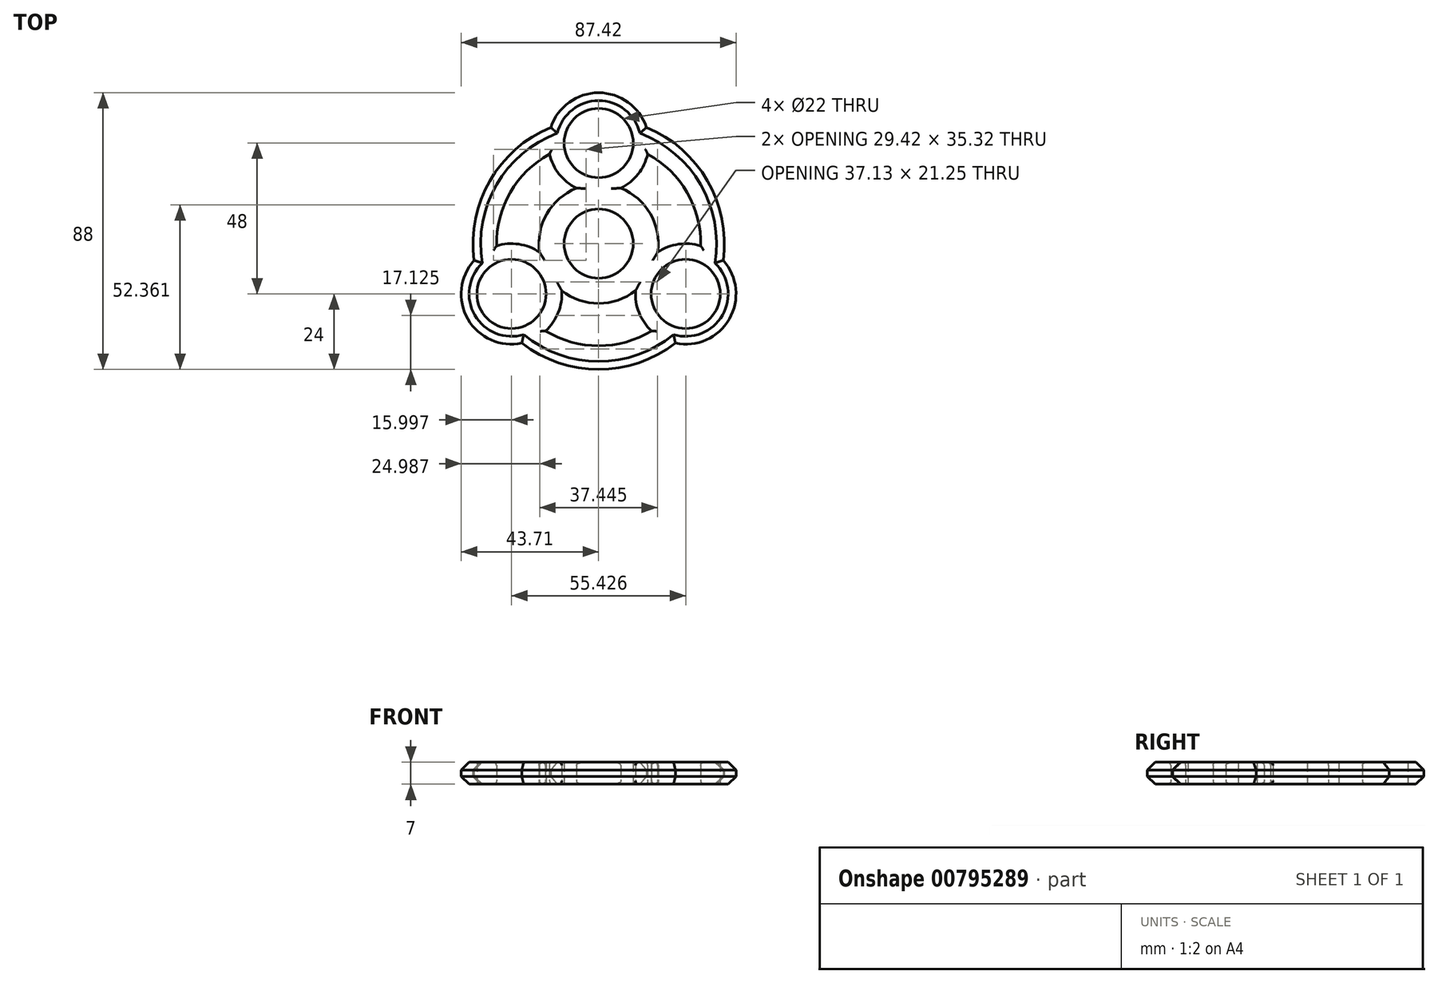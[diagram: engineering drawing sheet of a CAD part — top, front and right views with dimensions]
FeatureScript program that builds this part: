
annotation { "Feature Type Name" : "Feature", "Feature Type Description" : "" }
export const myFeature = defineFeature(function(context is Context, id is Id, definition is map)
    precondition{}
    {
        {
            var Q0;
            Q0=qCreatedBy(makeId("Top.planeOp"),FACE);
            var sketch = newSketch(context, id + "F0", { "sketchPlane" : qUnion([Q0])});
            skCircle(sketch, "E0", {"center": v(0, 0) * mm, "radius": 11 * mm});
            skCircle(sketch, "E1", {"center": v(0, 0) * mm, "radius": 19 * mm});
            skCircle(sketch, "E2", {"center": v(0, 0) * mm, "radius": 40 * mm});
            skCircle(sketch, "E3", {"center": v(0, 0) * mm, "radius": 32.5 * mm});
            skCircle(sketch, "E4", {"center": v(0, 32) * mm, "radius": 11 * mm});
            skCircle(sketch, "E5", {"center": v(0, 32) * mm, "radius": 16 * mm});
            skCircle(sketch, "E6.1.0", {"center": v(-27.71, -16) * mm, "radius": 16 * mm});
            skCircle(sketch, "E6.1.1", {"center": v(-27.71, -16) * mm, "radius": 11 * mm});
            skCircle(sketch, "E6.2.0", {"center": v(27.71, -16) * mm, "radius": 16 * mm});
            skCircle(sketch, "E6.2.1", {"center": v(27.71, -16) * mm, "radius": 11 * mm});
            skSolve(sketch);
        }
        {
            var Q0;
            {var subQ0=sQuery(id+"F0.wireOp",EDGE,"E6.1.0");var subQ1=sQuery(id+"F0.wireOp",EDGE,"E2");var subQ2=makeQuery(id+"F0.imprint","INTERSECT",VERTEX,{"disambiguationData":[OD(0.0)],"derivedFrom":[subQ1,subQ0]});Q0=makeQuery(id+"F0.imprint","IMPRINT",FACE,{"disambiguationData":[TD([[makeQuery(id+"F0.imprint","IMPRINT",EDGE,{"disambiguationData":[TD([[subQ2,-1.0]])],"derivedFrom":subQ1}),1.0]])]});}
            var Q1;
            {var subQ0=sQuery(id+"F0.wireOp",EDGE,"E6.1.0");var subQ1=sQuery(id+"F0.wireOp",EDGE,"E2");var subQ2=makeQuery(id+"F0.imprint","INTERSECT",VERTEX,{"disambiguationData":[OD(1.0)],"derivedFrom":[subQ1,subQ0]});Q1=makeQuery(id+"F0.imprint","IMPRINT",FACE,{"disambiguationData":[TD([[makeQuery(id+"F0.imprint","IMPRINT",EDGE,{"disambiguationData":[TD([[subQ2,1.0]])],"derivedFrom":subQ1}),1.0]])]});}
            var Q2;
            {var subQ0=sQuery(id+"F0.wireOp",EDGE,"E6.1.0");var subQ1=sQuery(id+"F0.wireOp",EDGE,"E2");var subQ2=makeQuery(id+"F0.imprint","INTERSECT",VERTEX,{"disambiguationData":[OD(1.0)],"derivedFrom":[subQ1,subQ0]});Q2=makeQuery(id+"F0.imprint","IMPRINT",FACE,{"disambiguationData":[TD([[makeQuery(id+"F0.imprint","IMPRINT",EDGE,{"disambiguationData":[TD([[subQ2,-1.0]])],"derivedFrom":subQ1}),1.0]])]});}
            var Q3;
            {var subQ0=sQuery(id+"F0.wireOp",EDGE,"E6.1.0");var subQ1=sQuery(id+"F0.wireOp",EDGE,"E2");var subQ2=makeQuery(id+"F0.imprint","INTERSECT",VERTEX,{"disambiguationData":[OD(0.0)],"derivedFrom":[subQ1,subQ0]});Q3=makeQuery(id+"F0.imprint","IMPRINT",FACE,{"disambiguationData":[TD([[makeQuery(id+"F0.imprint","IMPRINT",EDGE,{"disambiguationData":[TD([[subQ2,-1.0]])],"derivedFrom":subQ1}),-1.0]])]});}
            var Q4;
            {var subQ3=sQuery(id+"F0.wireOp",EDGE,"E6.1.0");var subQ5=sQuery(id+"F0.wireOp",EDGE,"E1");var subQ6=makeQuery(id+"F0.imprint","INTERSECT",VERTEX,{"disambiguationData":[OD(0.0)],"derivedFrom":[subQ5,subQ3]});Q4=makeQuery(id+"F0.imprint","IMPRINT",FACE,{"disambiguationData":[TD([[makeQuery(id+"F0.imprint","IMPRINT",EDGE,{"disambiguationData":[TD([[subQ6,-1.0]])],"derivedFrom":subQ5}),-1.0]])]});}
            var Q5;
            {var subQ0=sQuery(id+"F0.wireOp",EDGE,"E6.1.0");var subQ1=sQuery(id+"F0.wireOp",EDGE,"E1");var subQ2=makeQuery(id+"F0.imprint","INTERSECT",VERTEX,{"disambiguationData":[OD(0.0)],"derivedFrom":[subQ1,subQ0]});Q5=makeQuery(id+"F0.imprint","IMPRINT",FACE,{"disambiguationData":[TD([[makeQuery(id+"F0.imprint","IMPRINT",EDGE,{"disambiguationData":[TD([[subQ2,-1.0]])],"derivedFrom":subQ1}),1.0]])]});}
            var Q6;
            Q6=makeQuery(id+"F0.imprint","IMPRINT",FACE,{"disambiguationData":[TD([[makeQuery(id+"F0.imprint","IMPRINT",EDGE,{"derivedFrom":sQuery(id+"F0.wireOp",EDGE,"E0")}),-1.0]])]});
            var Q7;
            {var subQ0=sQuery(id+"F0.wireOp",EDGE,"E6.2.0");var subQ1=sQuery(id+"F0.wireOp",EDGE,"E1");var subQ2=makeQuery(id+"F0.imprint","INTERSECT",VERTEX,{"disambiguationData":[OD(0.0)],"derivedFrom":[subQ1,subQ0]});Q7=makeQuery(id+"F0.imprint","IMPRINT",FACE,{"disambiguationData":[TD([[makeQuery(id+"F0.imprint","IMPRINT",EDGE,{"disambiguationData":[TD([[subQ2,-1.0]])],"derivedFrom":subQ1}),1.0]])]});}
            var Q8;
            {var subQ0=sQuery(id+"F0.wireOp",EDGE,"E6.2.0");var subQ1=sQuery(id+"F0.wireOp",EDGE,"E1");var subQ9=makeQuery(id+"F0.imprint","INTERSECT",VERTEX,{"disambiguationData":[OD(0.0)],"derivedFrom":[subQ1,subQ0]});Q8=makeQuery(id+"F0.imprint","IMPRINT",FACE,{"disambiguationData":[TD([[makeQuery(id+"F0.imprint","IMPRINT",EDGE,{"disambiguationData":[TD([[subQ9,-1.0]])],"derivedFrom":subQ1}),-1.0]])]});}
            var Q9;
            {var subQ0=sQuery(id+"F0.wireOp",EDGE,"E6.2.0");var subQ1=sQuery(id+"F0.wireOp",EDGE,"E2");var subQ2=makeQuery(id+"F0.imprint","INTERSECT",VERTEX,{"disambiguationData":[OD(0.0)],"derivedFrom":[subQ1,subQ0]});Q9=makeQuery(id+"F0.imprint","IMPRINT",FACE,{"disambiguationData":[TD([[makeQuery(id+"F0.imprint","IMPRINT",EDGE,{"disambiguationData":[TD([[subQ2,-1.0]])],"derivedFrom":subQ1}),1.0]])]});}
            var Q10;
            {var subQ0=sQuery(id+"F0.wireOp",EDGE,"E6.2.0");var subQ1=sQuery(id+"F0.wireOp",EDGE,"E2");var subQ2=makeQuery(id+"F0.imprint","INTERSECT",VERTEX,{"disambiguationData":[OD(1.0)],"derivedFrom":[subQ1,subQ0]});Q10=makeQuery(id+"F0.imprint","IMPRINT",FACE,{"disambiguationData":[TD([[makeQuery(id+"F0.imprint","IMPRINT",EDGE,{"disambiguationData":[TD([[subQ2,1.0]])],"derivedFrom":subQ1}),1.0]])]});}
            var Q11;
            {var subQ0=sQuery(id+"F0.wireOp",EDGE,"E5");var subQ1=sQuery(id+"F0.wireOp",EDGE,"E2");var subQ2=makeQuery(id+"F0.imprint","INTERSECT",VERTEX,{"disambiguationData":[OD(0.0)],"derivedFrom":[subQ1,subQ0]});Q11=makeQuery(id+"F0.imprint","IMPRINT",FACE,{"disambiguationData":[TD([[makeQuery(id+"F0.imprint","IMPRINT",EDGE,{"disambiguationData":[TD([[subQ2,1.0]])],"derivedFrom":subQ1}),1.0]])]});}
            var Q12;
            {var subQ0=sQuery(id+"F0.wireOp",EDGE,"E6.2.0");var subQ1=sQuery(id+"F0.wireOp",EDGE,"E2");var subQ2=makeQuery(id+"F0.imprint","INTERSECT",VERTEX,{"disambiguationData":[OD(0.0)],"derivedFrom":[subQ1,subQ0]});Q12=makeQuery(id+"F0.imprint","IMPRINT",FACE,{"disambiguationData":[TD([[makeQuery(id+"F0.imprint","IMPRINT",EDGE,{"disambiguationData":[TD([[subQ2,-1.0]])],"derivedFrom":subQ1}),-1.0]])]});}
            var Q13;
            {var subQ0=sQuery(id+"F0.wireOp",EDGE,"E5");var subQ1=sQuery(id+"F0.wireOp",EDGE,"E1");var subQ2=makeQuery(id+"F0.imprint","INTERSECT",VERTEX,{"disambiguationData":[OD(0.0)],"derivedFrom":[subQ1,subQ0]});Q13=makeQuery(id+"F0.imprint","IMPRINT",FACE,{"disambiguationData":[TD([[makeQuery(id+"F0.imprint","IMPRINT",EDGE,{"disambiguationData":[TD([[subQ2,1.0]])],"derivedFrom":subQ1}),1.0]])]});}
            var Q14;
            {var subQ0=sQuery(id+"F0.wireOp",EDGE,"E5");var subQ1=sQuery(id+"F0.wireOp",EDGE,"E2");var subQ2=makeQuery(id+"F0.imprint","INTERSECT",VERTEX,{"disambiguationData":[OD(1.0)],"derivedFrom":[subQ1,subQ0]});Q14=makeQuery(id+"F0.imprint","IMPRINT",FACE,{"disambiguationData":[TD([[makeQuery(id+"F0.imprint","IMPRINT",EDGE,{"disambiguationData":[TD([[subQ2,-1.0]])],"derivedFrom":subQ1}),1.0]])]});}
            var Q15;
            {var subQ0=sQuery(id+"F0.wireOp",EDGE,"E5");var subQ1=sQuery(id+"F0.wireOp",EDGE,"E2");var subQ2=makeQuery(id+"F0.imprint","INTERSECT",VERTEX,{"disambiguationData":[OD(0.0)],"derivedFrom":[subQ1,subQ0]});Q15=makeQuery(id+"F0.imprint","IMPRINT",FACE,{"disambiguationData":[TD([[makeQuery(id+"F0.imprint","IMPRINT",EDGE,{"disambiguationData":[TD([[subQ2,-1.0]])],"derivedFrom":subQ1}),1.0]])]});}
            var Q16;
            {var subQ0=sQuery(id+"F0.wireOp",EDGE,"E5");var subQ1=sQuery(id+"F0.wireOp",EDGE,"E2");var subQ2=makeQuery(id+"F0.imprint","INTERSECT",VERTEX,{"disambiguationData":[OD(1.0)],"derivedFrom":[subQ1,subQ0]});Q16=makeQuery(id+"F0.imprint","IMPRINT",FACE,{"disambiguationData":[TD([[makeQuery(id+"F0.imprint","IMPRINT",EDGE,{"disambiguationData":[TD([[subQ2,1.0]])],"derivedFrom":subQ1}),1.0]])]});}
            var Q17;
            {var subQ0=sQuery(id+"F0.wireOp",EDGE,"E5");var subQ1=sQuery(id+"F0.wireOp",EDGE,"E2");var subQ2=makeQuery(id+"F0.imprint","INTERSECT",VERTEX,{"disambiguationData":[OD(0.0)],"derivedFrom":[subQ1,subQ0]});Q17=makeQuery(id+"F0.imprint","IMPRINT",FACE,{"disambiguationData":[TD([[makeQuery(id+"F0.imprint","IMPRINT",EDGE,{"disambiguationData":[TD([[subQ2,-1.0]])],"derivedFrom":subQ1}),-1.0]])]});}
            var Q18;
            {var subQ0=sQuery(id+"F0.wireOp",EDGE,"E5");var subQ1=sQuery(id+"F0.wireOp",EDGE,"E1");var subQ2=makeQuery(id+"F0.imprint","INTERSECT",VERTEX,{"disambiguationData":[OD(0.0)],"derivedFrom":[subQ1,subQ0]});Q18=makeQuery(id+"F0.imprint","IMPRINT",FACE,{"disambiguationData":[TD([[makeQuery(id+"F0.imprint","IMPRINT",EDGE,{"disambiguationData":[TD([[subQ2,-1.0]])],"derivedFrom":subQ1}),1.0]])]});}
            var Q19;
            {var subQ0=sQuery(id+"F0.wireOp",EDGE,"e3311fa9-2675-4763-9959-c69614a33db8.1.3.0");var subQ1=sQuery(id+"F0.wireOp",EDGE,"E1");var subQ2=makeQuery(id+"F0.imprint","INTERSECT",VERTEX,{"disambiguationData":[OD(0.0)],"derivedFrom":[subQ1,subQ0]});Q19=makeQuery(id+"F0.imprint","IMPRINT",FACE,{"disambiguationData":[TD([[makeQuery(id+"F0.imprint","IMPRINT",EDGE,{"disambiguationData":[TD([[subQ2,1.0]])],"derivedFrom":subQ1}),1.0]])]});}
            var Q20;
            {var subQ0=sQuery(id+"F0.wireOp",EDGE,"e3311fa9-2675-4763-9959-c69614a33db8.1.3.0");var subQ7=sQuery(id+"F0.wireOp",EDGE,"E1");var subQ8=makeQuery(id+"F0.imprint","INTERSECT",VERTEX,{"disambiguationData":[OD(0.0)],"derivedFrom":[subQ7,subQ0]});Q20=makeQuery(id+"F0.imprint","IMPRINT",FACE,{"disambiguationData":[TD([[makeQuery(id+"F0.imprint","IMPRINT",EDGE,{"disambiguationData":[TD([[subQ8,1.0]])],"derivedFrom":subQ7}),-1.0]])]});}
            var Q21;
            {var subQ0=sQuery(id+"F0.wireOp",EDGE,"e3311fa9-2675-4763-9959-c69614a33db8.1.3.0");var subQ1=sQuery(id+"F0.wireOp",EDGE,"E2");var subQ2=makeQuery(id+"F0.imprint","INTERSECT",VERTEX,{"disambiguationData":[OD(1.0)],"derivedFrom":[subQ1,subQ0]});Q21=makeQuery(id+"F0.imprint","IMPRINT",FACE,{"disambiguationData":[TD([[makeQuery(id+"F0.imprint","IMPRINT",EDGE,{"disambiguationData":[TD([[subQ2,-1.0]])],"derivedFrom":subQ1}),1.0]])]});}
            var Q22;
            {var subQ0=sQuery(id+"F0.wireOp",EDGE,"e3311fa9-2675-4763-9959-c69614a33db8.1.3.0");var subQ1=sQuery(id+"F0.wireOp",EDGE,"E2");var subQ2=makeQuery(id+"F0.imprint","INTERSECT",VERTEX,{"disambiguationData":[OD(0.0)],"derivedFrom":[subQ1,subQ0]});Q22=makeQuery(id+"F0.imprint","IMPRINT",FACE,{"disambiguationData":[TD([[makeQuery(id+"F0.imprint","IMPRINT",EDGE,{"disambiguationData":[TD([[subQ2,1.0]])],"derivedFrom":subQ1}),1.0]])]});}
            var Q23;
            {var subQ0=sQuery(id+"F0.wireOp",EDGE,"e3311fa9-2675-4763-9959-c69614a33db8.1.3.0");var subQ1=sQuery(id+"F0.wireOp",EDGE,"E2");var subQ2=makeQuery(id+"F0.imprint","INTERSECT",VERTEX,{"disambiguationData":[OD(0.0)],"derivedFrom":[subQ1,subQ0]});Q23=makeQuery(id+"F0.imprint","IMPRINT",FACE,{"disambiguationData":[TD([[makeQuery(id+"F0.imprint","IMPRINT",EDGE,{"disambiguationData":[TD([[subQ2,1.0]])],"derivedFrom":subQ1}),-1.0]])]});}
            var Q24;
            {var subQ0=sQuery(id+"F0.wireOp",EDGE,"E6.2.0");var subQ1=sQuery(id+"F0.wireOp",EDGE,"E2");var subQ2=makeQuery(id+"F0.imprint","INTERSECT",VERTEX,{"disambiguationData":[OD(1.0)],"derivedFrom":[subQ1,subQ0]});Q24=makeQuery(id+"F0.imprint","IMPRINT",FACE,{"disambiguationData":[TD([[makeQuery(id+"F0.imprint","IMPRINT",EDGE,{"disambiguationData":[TD([[subQ2,-1.0]])],"derivedFrom":subQ1}),1.0]])]});}
            var Q25;
            {var subQ4=sQuery(id+"F0.wireOp",EDGE,"E5");var subQ7=sQuery(id+"F0.wireOp",EDGE,"E1");var subQ8=makeQuery(id+"F0.imprint","INTERSECT",VERTEX,{"disambiguationData":[OD(0.0)],"derivedFrom":[subQ7,subQ4]});Q25=makeQuery(id+"F0.imprint","IMPRINT",FACE,{"disambiguationData":[TD([[makeQuery(id+"F0.imprint","IMPRINT",EDGE,{"disambiguationData":[TD([[subQ8,1.0]])],"derivedFrom":subQ7}),-1.0]])]});}
            extrude(context, id + "F1", {"entities" : qUnion([Q0, Q1, Q2, Q3, Q4, Q5, Q6, Q7, Q8, Q9, Q10, Q11, Q12, Q13, Q14, Q15, Q16, Q17, Q18, Q19, Q20, Q21, Q22, Q23, Q24, Q25]), "depth" : 7 * mm, "offsetDistance" : 25 * mm});
        }
        {
            var Q0;
            {var subQ0=sQuery(id+"F0.wireOp",EDGE,"E2");Q0=makeQuery(id+"F1.opExtrude","CAP_EDGE",EDGE,{"disambiguationData":[OSD([subQ0]),TDD([makeQuery(id+"F0.imprint","IMPRINT",EDGE,{"disambiguationData":[TD([[makeQuery(id+"F0.imprint","INTERSECT",VERTEX,{"disambiguationData":[OD(1.0)],"derivedFrom":[subQ0,sQuery(id+"F0.wireOp",EDGE,"E6.1.0")]}),-1.0]])],"derivedFrom":subQ0})])],"isStart":false});}
            var Q1;
            {var subQ0=sQuery(id+"F0.wireOp",EDGE,"E2");Q1=makeQuery(id+"F1.opExtrude","CAP_EDGE",EDGE,{"disambiguationData":[OSD([subQ0]),TDD([makeQuery(id+"F0.imprint","IMPRINT",EDGE,{"disambiguationData":[TD([[makeQuery(id+"F0.imprint","INTERSECT",VERTEX,{"disambiguationData":[OD(1.0)],"derivedFrom":[subQ0,sQuery(id+"F0.wireOp",EDGE,"E5")]}),-1.0]])],"derivedFrom":subQ0})])],"isStart":false});}
            var Q2;
            {var subQ0=sQuery(id+"F0.wireOp",EDGE,"E6.1.0");var subQ1=sQuery(id+"F0.wireOp",EDGE,"E2");Q2=makeQuery(id+"F1.opExtrude","CAP_EDGE",EDGE,{"disambiguationData":[OSD([subQ0]),TDD([makeQuery(id+"F0.imprint","IMPRINT",EDGE,{"disambiguationData":[TD([[makeQuery(id+"F0.imprint","INTERSECT",VERTEX,{"disambiguationData":[OD(0.0)],"derivedFrom":[subQ1,subQ0]}),-1.0]])],"derivedFrom":subQ0})])],"isStart":false});}
            var Q3;
            {var subQ0=sQuery(id+"F0.wireOp",EDGE,"E5");var subQ1=sQuery(id+"F0.wireOp",EDGE,"E2");Q3=makeQuery(id+"F1.opExtrude","CAP_EDGE",EDGE,{"disambiguationData":[OSD([subQ0]),TDD([makeQuery(id+"F0.imprint","IMPRINT",EDGE,{"disambiguationData":[TD([[makeQuery(id+"F0.imprint","INTERSECT",VERTEX,{"disambiguationData":[OD(0.0)],"derivedFrom":[subQ1,subQ0]}),-1.0]])],"derivedFrom":subQ0})])],"isStart":false});}
            var Q4;
            {var subQ0=sQuery(id+"F0.wireOp",EDGE,"E6.2.0");var subQ1=sQuery(id+"F0.wireOp",EDGE,"E2");Q4=makeQuery(id+"F1.opExtrude","CAP_EDGE",EDGE,{"disambiguationData":[OSD([subQ0]),TDD([makeQuery(id+"F0.imprint","IMPRINT",EDGE,{"disambiguationData":[TD([[makeQuery(id+"F0.imprint","INTERSECT",VERTEX,{"disambiguationData":[OD(0.0)],"derivedFrom":[subQ1,subQ0]}),-1.0]])],"derivedFrom":subQ0})])],"isStart":false});}
            var Q5;
            {var subQ0=sQuery(id+"F0.wireOp",EDGE,"E2");Q5=makeQuery(id+"F1.opExtrude","CAP_EDGE",EDGE,{"disambiguationData":[OSD([subQ0]),TDD([makeQuery(id+"F0.imprint","IMPRINT",EDGE,{"disambiguationData":[TD([[makeQuery(id+"F0.imprint","INTERSECT",VERTEX,{"disambiguationData":[OD(0.0)],"derivedFrom":[subQ0,sQuery(id+"F0.wireOp",EDGE,"E5")]}),1.0]])],"derivedFrom":subQ0})])],"isStart":false});}
            var Q6;
            {var subQ0=sQuery(id+"F0.wireOp",EDGE,"E2");Q6=makeQuery(id+"F1.opExtrude","CAP_EDGE",EDGE,{"disambiguationData":[OSD([subQ0]),TDD([makeQuery(id+"F0.imprint","IMPRINT",EDGE,{"disambiguationData":[TD([[makeQuery(id+"F0.imprint","INTERSECT",VERTEX,{"disambiguationData":[OD(0.0)],"derivedFrom":[subQ0,sQuery(id+"F0.wireOp",EDGE,"E5")]}),1.0]])],"derivedFrom":subQ0})])],"isStart":true});}
            var Q7;
            {var subQ0=sQuery(id+"F0.wireOp",EDGE,"E6.2.0");var subQ1=sQuery(id+"F0.wireOp",EDGE,"E2");Q7=makeQuery(id+"F1.opExtrude","CAP_EDGE",EDGE,{"disambiguationData":[OSD([subQ0]),TDD([makeQuery(id+"F0.imprint","IMPRINT",EDGE,{"disambiguationData":[TD([[makeQuery(id+"F0.imprint","INTERSECT",VERTEX,{"disambiguationData":[OD(0.0)],"derivedFrom":[subQ1,subQ0]}),-1.0]])],"derivedFrom":subQ0})])],"isStart":true});}
            var Q8;
            {var subQ0=sQuery(id+"F0.wireOp",EDGE,"E2");Q8=makeQuery(id+"F1.opExtrude","CAP_EDGE",EDGE,{"disambiguationData":[OSD([subQ0]),TDD([makeQuery(id+"F0.imprint","IMPRINT",EDGE,{"disambiguationData":[TD([[makeQuery(id+"F0.imprint","INTERSECT",VERTEX,{"disambiguationData":[OD(1.0)],"derivedFrom":[subQ0,sQuery(id+"F0.wireOp",EDGE,"E6.1.0")]}),-1.0]])],"derivedFrom":subQ0})])],"isStart":true});}
            var Q9;
            {var subQ0=sQuery(id+"F0.wireOp",EDGE,"E6.1.0");var subQ1=sQuery(id+"F0.wireOp",EDGE,"E2");Q9=makeQuery(id+"F1.opExtrude","CAP_EDGE",EDGE,{"disambiguationData":[OSD([subQ0]),TDD([makeQuery(id+"F0.imprint","IMPRINT",EDGE,{"disambiguationData":[TD([[makeQuery(id+"F0.imprint","INTERSECT",VERTEX,{"disambiguationData":[OD(0.0)],"derivedFrom":[subQ1,subQ0]}),-1.0]])],"derivedFrom":subQ0})])],"isStart":true});}
            var Q10;
            {var subQ0=sQuery(id+"F0.wireOp",EDGE,"E2");Q10=makeQuery(id+"F1.opExtrude","CAP_EDGE",EDGE,{"disambiguationData":[OSD([subQ0]),TDD([makeQuery(id+"F0.imprint","IMPRINT",EDGE,{"disambiguationData":[TD([[makeQuery(id+"F0.imprint","INTERSECT",VERTEX,{"disambiguationData":[OD(1.0)],"derivedFrom":[subQ0,sQuery(id+"F0.wireOp",EDGE,"E5")]}),-1.0]])],"derivedFrom":subQ0})])],"isStart":true});}
            var Q11;
            {var subQ0=sQuery(id+"F0.wireOp",EDGE,"E5");var subQ1=sQuery(id+"F0.wireOp",EDGE,"E2");Q11=makeQuery(id+"F1.opExtrude","CAP_EDGE",EDGE,{"disambiguationData":[OSD([subQ0]),TDD([makeQuery(id+"F0.imprint","IMPRINT",EDGE,{"disambiguationData":[TD([[makeQuery(id+"F0.imprint","INTERSECT",VERTEX,{"disambiguationData":[OD(0.0)],"derivedFrom":[subQ1,subQ0]}),-1.0]])],"derivedFrom":subQ0})])],"isStart":true});}
            var Q12;
            {var subQ0=sQuery(id+"F0.wireOp",EDGE,"E2");Q12=makeQuery(id+"F1.opExtrude","CAP_EDGE",EDGE,{"disambiguationData":[OSD([subQ0]),TDD([makeQuery(id+"F0.imprint","IMPRINT",EDGE,{"disambiguationData":[TD([[makeQuery(id+"F0.imprint","INTERSECT",VERTEX,{"disambiguationData":[OD(1.0)],"derivedFrom":[subQ0,sQuery(id+"F0.wireOp",EDGE,"E6.2.0")]}),-1.0]])],"derivedFrom":subQ0})])],"isStart":false});}
            var Q13;
            {var subQ0=sQuery(id+"F0.wireOp",EDGE,"E2");Q13=makeQuery(id+"F1.opExtrude","CAP_EDGE",EDGE,{"disambiguationData":[OSD([subQ0]),TDD([makeQuery(id+"F0.imprint","IMPRINT",EDGE,{"disambiguationData":[TD([[makeQuery(id+"F0.imprint","INTERSECT",VERTEX,{"disambiguationData":[OD(1.0)],"derivedFrom":[subQ0,sQuery(id+"F0.wireOp",EDGE,"E6.2.0")]}),-1.0]])],"derivedFrom":subQ0})])],"isStart":true});}
            var Q14;
            {var subQ0=sQuery(id+"F0.wireOp",EDGE,"e3311fa9-2675-4763-9959-c69614a33db8.1.3.0");var subQ1=sQuery(id+"F0.wireOp",EDGE,"E2");Q14=makeQuery(id+"F1.opExtrude","CAP_EDGE",EDGE,{"disambiguationData":[OSD([subQ0]),TDD([makeQuery(id+"F0.imprint","IMPRINT",EDGE,{"disambiguationData":[TD([[makeQuery(id+"F0.imprint","INTERSECT",VERTEX,{"disambiguationData":[OD(0.0)],"derivedFrom":[subQ1,subQ0]}),1.0]])],"derivedFrom":subQ0})])],"isStart":false});}
            var Q15;
            {var subQ0=sQuery(id+"F0.wireOp",EDGE,"e3311fa9-2675-4763-9959-c69614a33db8.1.3.0");var subQ1=sQuery(id+"F0.wireOp",EDGE,"E2");Q15=makeQuery(id+"F1.opExtrude","CAP_EDGE",EDGE,{"disambiguationData":[OSD([subQ0]),TDD([makeQuery(id+"F0.imprint","IMPRINT",EDGE,{"disambiguationData":[TD([[makeQuery(id+"F0.imprint","INTERSECT",VERTEX,{"disambiguationData":[OD(0.0)],"derivedFrom":[subQ1,subQ0]}),1.0]])],"derivedFrom":subQ0})])],"isStart":true});}
            chamfer(context, id + "F2", {"entities" : qUnion([Q0, Q1, Q2, Q3, Q4, Q5, Q6, Q7, Q8, Q9, Q10, Q11, Q12, Q13, Q14, Q15]), "width" : 2.5 * mm, "tangentPropagation" : true});
        }
        {
            var Q0;
            {var subQ0=sQuery(id+"F0.wireOp",EDGE,"E3");Q0=makeQuery(id+"F1.opExtrude","CAP_EDGE",EDGE,{"disambiguationData":[OSD([subQ0]),TDD([makeQuery(id+"F0.imprint","IMPRINT",EDGE,{"disambiguationData":[TD([[makeQuery(id+"F0.imprint","INTERSECT",VERTEX,{"disambiguationData":[OD(1.0)],"derivedFrom":[subQ0,sQuery(id+"F0.wireOp",EDGE,"E6.1.0")]}),-1.0]])],"derivedFrom":subQ0})])],"isStart":false});}
            var Q1;
            {var subQ0=sQuery(id+"F0.wireOp",EDGE,"E6.1.0");Q1=makeQuery(id+"F1.opExtrude","CAP_EDGE",EDGE,{"disambiguationData":[OSD([subQ0]),TDD([makeQuery(id+"F0.imprint","IMPRINT",EDGE,{"disambiguationData":[TD([[makeQuery(id+"F0.imprint","INTERSECT",VERTEX,{"disambiguationData":[OD(1.0)],"derivedFrom":[sQuery(id+"F0.wireOp",EDGE,"E1"),subQ0]}),1.0]])],"derivedFrom":subQ0})])],"isStart":false});}
            var Q2;
            {var subQ0=sQuery(id+"F0.wireOp",EDGE,"E1");Q2=makeQuery(id+"F1.opExtrude","CAP_EDGE",EDGE,{"disambiguationData":[OSD([subQ0]),TDD([makeQuery(id+"F0.imprint","IMPRINT",EDGE,{"disambiguationData":[TD([[makeQuery(id+"F0.imprint","INTERSECT",VERTEX,{"disambiguationData":[OD(1.0)],"derivedFrom":[subQ0,sQuery(id+"F0.wireOp",EDGE,"E6.1.0")]}),-1.0]])],"derivedFrom":subQ0})])],"isStart":false});}
            var Q3;
            {var subQ0=sQuery(id+"F0.wireOp",EDGE,"E6.2.0");Q3=makeQuery(id+"F1.opExtrude","CAP_EDGE",EDGE,{"disambiguationData":[OSD([subQ0]),TDD([makeQuery(id+"F0.imprint","IMPRINT",EDGE,{"disambiguationData":[TD([[makeQuery(id+"F0.imprint","INTERSECT",VERTEX,{"disambiguationData":[OD(0.0)],"derivedFrom":[sQuery(id+"F0.wireOp",EDGE,"E1"),subQ0]}),-1.0]])],"derivedFrom":subQ0})])],"isStart":false});}
            var Q4;
            {var subQ0=sQuery(id+"F0.wireOp",EDGE,"E1");Q4=makeQuery(id+"F1.opExtrude","CAP_EDGE",EDGE,{"disambiguationData":[OSD([subQ0]),TDD([makeQuery(id+"F0.imprint","IMPRINT",EDGE,{"disambiguationData":[TD([[makeQuery(id+"F0.imprint","INTERSECT",VERTEX,{"disambiguationData":[OD(1.0)],"derivedFrom":[subQ0,sQuery(id+"F0.wireOp",EDGE,"E5")]}),1.0]])],"derivedFrom":subQ0})])],"isStart":false});}
            var Q5;
            {var subQ0=sQuery(id+"F0.wireOp",EDGE,"E5");Q5=makeQuery(id+"F1.opExtrude","CAP_EDGE",EDGE,{"disambiguationData":[OSD([subQ0]),TDD([makeQuery(id+"F0.imprint","IMPRINT",EDGE,{"disambiguationData":[TD([[makeQuery(id+"F0.imprint","INTERSECT",VERTEX,{"disambiguationData":[OD(1.0)],"derivedFrom":[sQuery(id+"F0.wireOp",EDGE,"E1"),subQ0]}),-1.0]])],"derivedFrom":subQ0})])],"isStart":false});}
            var Q6;
            {var subQ0=sQuery(id+"F0.wireOp",EDGE,"E3");Q6=makeQuery(id+"F1.opExtrude","CAP_EDGE",EDGE,{"disambiguationData":[OSD([subQ0]),TDD([makeQuery(id+"F0.imprint","IMPRINT",EDGE,{"disambiguationData":[TD([[makeQuery(id+"F0.imprint","INTERSECT",VERTEX,{"disambiguationData":[OD(0.0)],"derivedFrom":[subQ0,sQuery(id+"F0.wireOp",EDGE,"E5")]}),1.0]])],"derivedFrom":subQ0})])],"isStart":false});}
            var Q7;
            {var subQ0=sQuery(id+"F0.wireOp",EDGE,"E6.2.0");Q7=makeQuery(id+"F1.opExtrude","CAP_EDGE",EDGE,{"disambiguationData":[OSD([subQ0]),TDD([makeQuery(id+"F0.imprint","IMPRINT",EDGE,{"disambiguationData":[TD([[makeQuery(id+"F0.imprint","INTERSECT",VERTEX,{"disambiguationData":[OD(1.0)],"derivedFrom":[sQuery(id+"F0.wireOp",EDGE,"E1"),subQ0]}),1.0]])],"derivedFrom":subQ0})])],"isStart":false});}
            var Q8;
            {var subQ0=sQuery(id+"F0.wireOp",EDGE,"E6.1.0");Q8=makeQuery(id+"F1.opExtrude","CAP_EDGE",EDGE,{"disambiguationData":[OSD([subQ0]),TDD([makeQuery(id+"F0.imprint","IMPRINT",EDGE,{"disambiguationData":[TD([[makeQuery(id+"F0.imprint","INTERSECT",VERTEX,{"disambiguationData":[OD(0.0)],"derivedFrom":[sQuery(id+"F0.wireOp",EDGE,"E1"),subQ0]}),-1.0]])],"derivedFrom":subQ0})])],"isStart":false});}
            var Q9;
            {var subQ0=sQuery(id+"F0.wireOp",EDGE,"E1");Q9=makeQuery(id+"F1.opExtrude","CAP_EDGE",EDGE,{"disambiguationData":[OSD([subQ0]),TDD([makeQuery(id+"F0.imprint","IMPRINT",EDGE,{"disambiguationData":[TD([[makeQuery(id+"F0.imprint","INTERSECT",VERTEX,{"disambiguationData":[OD(0.0)],"derivedFrom":[subQ0,sQuery(id+"F0.wireOp",EDGE,"E5")]}),-1.0]])],"derivedFrom":subQ0})])],"isStart":false});}
            var Q10;
            {var subQ0=sQuery(id+"F0.wireOp",EDGE,"E5");Q10=makeQuery(id+"F1.opExtrude","CAP_EDGE",EDGE,{"disambiguationData":[OSD([subQ0]),TDD([makeQuery(id+"F0.imprint","IMPRINT",EDGE,{"disambiguationData":[TD([[makeQuery(id+"F0.imprint","INTERSECT",VERTEX,{"disambiguationData":[OD(0.0)],"derivedFrom":[sQuery(id+"F0.wireOp",EDGE,"E1"),subQ0]}),1.0]])],"derivedFrom":subQ0})])],"isStart":false});}
            var Q11;
            {var subQ0=sQuery(id+"F0.wireOp",EDGE,"E3");Q11=makeQuery(id+"F1.opExtrude","CAP_EDGE",EDGE,{"disambiguationData":[OSD([subQ0]),TDD([makeQuery(id+"F0.imprint","IMPRINT",EDGE,{"disambiguationData":[TD([[makeQuery(id+"F0.imprint","INTERSECT",VERTEX,{"disambiguationData":[OD(1.0)],"derivedFrom":[subQ0,sQuery(id+"F0.wireOp",EDGE,"E5")]}),-1.0]])],"derivedFrom":subQ0})])],"isStart":false});}
            var Q12;
            {var subQ0=sQuery(id+"F0.wireOp",EDGE,"E3");Q12=makeQuery(id+"F1.opExtrude","CAP_EDGE",EDGE,{"disambiguationData":[OSD([subQ0]),TDD([makeQuery(id+"F0.imprint","IMPRINT",EDGE,{"disambiguationData":[TD([[makeQuery(id+"F0.imprint","INTERSECT",VERTEX,{"disambiguationData":[OD(1.0)],"derivedFrom":[subQ0,sQuery(id+"F0.wireOp",EDGE,"E5")]}),-1.0]])],"derivedFrom":subQ0})])],"isStart":true});}
            var Q13;
            {var subQ0=sQuery(id+"F0.wireOp",EDGE,"E5");Q13=makeQuery(id+"F1.opExtrude","CAP_EDGE",EDGE,{"disambiguationData":[OSD([subQ0]),TDD([makeQuery(id+"F0.imprint","IMPRINT",EDGE,{"disambiguationData":[TD([[makeQuery(id+"F0.imprint","INTERSECT",VERTEX,{"disambiguationData":[OD(0.0)],"derivedFrom":[sQuery(id+"F0.wireOp",EDGE,"E1"),subQ0]}),1.0]])],"derivedFrom":subQ0})])],"isStart":true});}
            var Q14;
            {var subQ0=sQuery(id+"F0.wireOp",EDGE,"E1");Q14=makeQuery(id+"F1.opExtrude","CAP_EDGE",EDGE,{"disambiguationData":[OSD([subQ0]),TDD([makeQuery(id+"F0.imprint","IMPRINT",EDGE,{"disambiguationData":[TD([[makeQuery(id+"F0.imprint","INTERSECT",VERTEX,{"disambiguationData":[OD(0.0)],"derivedFrom":[subQ0,sQuery(id+"F0.wireOp",EDGE,"E5")]}),-1.0]])],"derivedFrom":subQ0})])],"isStart":true});}
            var Q15;
            {var subQ0=sQuery(id+"F0.wireOp",EDGE,"E6.1.0");Q15=makeQuery(id+"F1.opExtrude","CAP_EDGE",EDGE,{"disambiguationData":[OSD([subQ0]),TDD([makeQuery(id+"F0.imprint","IMPRINT",EDGE,{"disambiguationData":[TD([[makeQuery(id+"F0.imprint","INTERSECT",VERTEX,{"disambiguationData":[OD(0.0)],"derivedFrom":[sQuery(id+"F0.wireOp",EDGE,"E1"),subQ0]}),-1.0]])],"derivedFrom":subQ0})])],"isStart":true});}
            var Q16;
            {var subQ0=sQuery(id+"F0.wireOp",EDGE,"E3");Q16=makeQuery(id+"F1.opExtrude","CAP_EDGE",EDGE,{"disambiguationData":[OSD([subQ0]),TDD([makeQuery(id+"F0.imprint","IMPRINT",EDGE,{"disambiguationData":[TD([[makeQuery(id+"F0.imprint","INTERSECT",VERTEX,{"disambiguationData":[OD(1.0)],"derivedFrom":[subQ0,sQuery(id+"F0.wireOp",EDGE,"E6.1.0")]}),-1.0]])],"derivedFrom":subQ0})])],"isStart":true});}
            var Q17;
            {var subQ0=sQuery(id+"F0.wireOp",EDGE,"E6.1.0");Q17=makeQuery(id+"F1.opExtrude","CAP_EDGE",EDGE,{"disambiguationData":[OSD([subQ0]),TDD([makeQuery(id+"F0.imprint","IMPRINT",EDGE,{"disambiguationData":[TD([[makeQuery(id+"F0.imprint","INTERSECT",VERTEX,{"disambiguationData":[OD(1.0)],"derivedFrom":[sQuery(id+"F0.wireOp",EDGE,"E1"),subQ0]}),1.0]])],"derivedFrom":subQ0})])],"isStart":true});}
            var Q18;
            {var subQ0=sQuery(id+"F0.wireOp",EDGE,"E6.2.0");Q18=makeQuery(id+"F1.opExtrude","CAP_EDGE",EDGE,{"disambiguationData":[OSD([subQ0]),TDD([makeQuery(id+"F0.imprint","IMPRINT",EDGE,{"disambiguationData":[TD([[makeQuery(id+"F0.imprint","INTERSECT",VERTEX,{"disambiguationData":[OD(0.0)],"derivedFrom":[sQuery(id+"F0.wireOp",EDGE,"E1"),subQ0]}),-1.0]])],"derivedFrom":subQ0})])],"isStart":true});}
            var Q19;
            {var subQ0=sQuery(id+"F0.wireOp",EDGE,"E1");Q19=makeQuery(id+"F1.opExtrude","CAP_EDGE",EDGE,{"disambiguationData":[OSD([subQ0]),TDD([makeQuery(id+"F0.imprint","IMPRINT",EDGE,{"disambiguationData":[TD([[makeQuery(id+"F0.imprint","INTERSECT",VERTEX,{"disambiguationData":[OD(1.0)],"derivedFrom":[subQ0,sQuery(id+"F0.wireOp",EDGE,"E6.1.0")]}),-1.0]])],"derivedFrom":subQ0})])],"isStart":true});}
            var Q20;
            {var subQ0=sQuery(id+"F0.wireOp",EDGE,"E1");Q20=makeQuery(id+"F1.opExtrude","CAP_EDGE",EDGE,{"disambiguationData":[OSD([subQ0]),TDD([makeQuery(id+"F0.imprint","IMPRINT",EDGE,{"disambiguationData":[TD([[makeQuery(id+"F0.imprint","INTERSECT",VERTEX,{"disambiguationData":[OD(1.0)],"derivedFrom":[subQ0,sQuery(id+"F0.wireOp",EDGE,"E5")]}),1.0]])],"derivedFrom":subQ0})])],"isStart":true});}
            var Q21;
            {var subQ0=sQuery(id+"F0.wireOp",EDGE,"E5");Q21=makeQuery(id+"F1.opExtrude","CAP_EDGE",EDGE,{"disambiguationData":[OSD([subQ0]),TDD([makeQuery(id+"F0.imprint","IMPRINT",EDGE,{"disambiguationData":[TD([[makeQuery(id+"F0.imprint","INTERSECT",VERTEX,{"disambiguationData":[OD(1.0)],"derivedFrom":[sQuery(id+"F0.wireOp",EDGE,"E1"),subQ0]}),-1.0]])],"derivedFrom":subQ0})])],"isStart":true});}
            var Q22;
            {var subQ0=sQuery(id+"F0.wireOp",EDGE,"E3");Q22=makeQuery(id+"F1.opExtrude","CAP_EDGE",EDGE,{"disambiguationData":[OSD([subQ0]),TDD([makeQuery(id+"F0.imprint","IMPRINT",EDGE,{"disambiguationData":[TD([[makeQuery(id+"F0.imprint","INTERSECT",VERTEX,{"disambiguationData":[OD(0.0)],"derivedFrom":[subQ0,sQuery(id+"F0.wireOp",EDGE,"E5")]}),1.0]])],"derivedFrom":subQ0})])],"isStart":true});}
            var Q23;
            {var subQ0=sQuery(id+"F0.wireOp",EDGE,"E6.2.0");Q23=makeQuery(id+"F1.opExtrude","CAP_EDGE",EDGE,{"disambiguationData":[OSD([subQ0]),TDD([makeQuery(id+"F0.imprint","IMPRINT",EDGE,{"disambiguationData":[TD([[makeQuery(id+"F0.imprint","INTERSECT",VERTEX,{"disambiguationData":[OD(1.0)],"derivedFrom":[sQuery(id+"F0.wireOp",EDGE,"E1"),subQ0]}),1.0]])],"derivedFrom":subQ0})])],"isStart":true});}
            var Q24;
            {var subQ0=sQuery(id+"F0.wireOp",EDGE,"E1");Q24=makeQuery(id+"F1.opExtrude","CAP_EDGE",EDGE,{"disambiguationData":[OSD([subQ0]),TDD([makeQuery(id+"F0.imprint","IMPRINT",EDGE,{"disambiguationData":[TD([[makeQuery(id+"F0.imprint","INTERSECT",VERTEX,{"disambiguationData":[OD(0.0)],"derivedFrom":[subQ0,sQuery(id+"F0.wireOp",EDGE,"E5")]}),1.0]])],"derivedFrom":subQ0})])],"isStart":false});}
            var Q25;
            {var subQ0=sQuery(id+"F0.wireOp",EDGE,"E1");Q25=makeQuery(id+"F1.opExtrude","CAP_EDGE",EDGE,{"disambiguationData":[OSD([subQ0]),TDD([makeQuery(id+"F0.imprint","IMPRINT",EDGE,{"disambiguationData":[TD([[makeQuery(id+"F0.imprint","INTERSECT",VERTEX,{"disambiguationData":[OD(0.0)],"derivedFrom":[subQ0,sQuery(id+"F0.wireOp",EDGE,"E5")]}),1.0]])],"derivedFrom":subQ0})])],"isStart":true});}
            var Q26;
            {var subQ0=sQuery(id+"F0.wireOp",EDGE,"E5");Q26=makeQuery(id+"F1.opExtrude","CAP_EDGE",EDGE,{"disambiguationData":[OSD([subQ0]),TDD([makeQuery(id+"F0.imprint","IMPRINT",EDGE,{"disambiguationData":[TD([[makeQuery(id+"F0.imprint","INTERSECT",VERTEX,{"disambiguationData":[OD(0.0)],"derivedFrom":[sQuery(id+"F0.wireOp",EDGE,"E1"),subQ0]}),-1.0]])],"derivedFrom":subQ0})])],"isStart":false});}
            var Q27;
            {var subQ0=sQuery(id+"F0.wireOp",EDGE,"e3311fa9-2675-4763-9959-c69614a33db8.1.3.0");Q27=makeQuery(id+"F1.opExtrude","CAP_EDGE",EDGE,{"disambiguationData":[OSD([subQ0]),TDD([makeQuery(id+"F0.imprint","IMPRINT",EDGE,{"disambiguationData":[TD([[makeQuery(id+"F0.imprint","INTERSECT",VERTEX,{"disambiguationData":[OD(0.0)],"derivedFrom":[sQuery(id+"F0.wireOp",EDGE,"E1"),subQ0]}),1.0]])],"derivedFrom":subQ0})])],"isStart":false});}
            var Q28;
            {var subQ0=sQuery(id+"F0.wireOp",EDGE,"E5");Q28=makeQuery(id+"F1.opExtrude","CAP_EDGE",EDGE,{"disambiguationData":[OSD([subQ0]),TDD([makeQuery(id+"F0.imprint","IMPRINT",EDGE,{"disambiguationData":[TD([[makeQuery(id+"F0.imprint","INTERSECT",VERTEX,{"disambiguationData":[OD(0.0)],"derivedFrom":[sQuery(id+"F0.wireOp",EDGE,"E1"),subQ0]}),-1.0]])],"derivedFrom":subQ0})])],"isStart":true});}
            var Q29;
            {var subQ0=sQuery(id+"F0.wireOp",EDGE,"e3311fa9-2675-4763-9959-c69614a33db8.1.3.0");Q29=makeQuery(id+"F1.opExtrude","CAP_EDGE",EDGE,{"disambiguationData":[OSD([subQ0]),TDD([makeQuery(id+"F0.imprint","IMPRINT",EDGE,{"disambiguationData":[TD([[makeQuery(id+"F0.imprint","INTERSECT",VERTEX,{"disambiguationData":[OD(0.0)],"derivedFrom":[sQuery(id+"F0.wireOp",EDGE,"E1"),subQ0]}),1.0]])],"derivedFrom":subQ0})])],"isStart":true});}
            var Q30;
            {var subQ0=sQuery(id+"F0.wireOp",EDGE,"E1");Q30=makeQuery(id+"F1.opExtrude","CAP_EDGE",EDGE,{"disambiguationData":[OSD([subQ0]),TDD([makeQuery(id+"F0.imprint","IMPRINT",EDGE,{"disambiguationData":[TD([[makeQuery(id+"F0.imprint","INTERSECT",VERTEX,{"disambiguationData":[OD(1.0)],"derivedFrom":[subQ0,sQuery(id+"F0.wireOp",EDGE,"E6.2.0")]}),-1.0]])],"derivedFrom":subQ0})])],"isStart":false});}
            var Q31;
            {var subQ0=sQuery(id+"F0.wireOp",EDGE,"e3311fa9-2675-4763-9959-c69614a33db8.1.3.0");Q31=makeQuery(id+"F1.opExtrude","CAP_EDGE",EDGE,{"disambiguationData":[OSD([subQ0]),TDD([makeQuery(id+"F0.imprint","IMPRINT",EDGE,{"disambiguationData":[TD([[makeQuery(id+"F0.imprint","INTERSECT",VERTEX,{"disambiguationData":[OD(1.0)],"derivedFrom":[sQuery(id+"F0.wireOp",EDGE,"E1"),subQ0]}),-1.0]])],"derivedFrom":subQ0})])],"isStart":false});}
            var Q32;
            {var subQ0=sQuery(id+"F0.wireOp",EDGE,"E3");Q32=makeQuery(id+"F1.opExtrude","CAP_EDGE",EDGE,{"disambiguationData":[OSD([subQ0]),TDD([makeQuery(id+"F0.imprint","IMPRINT",EDGE,{"disambiguationData":[TD([[makeQuery(id+"F0.imprint","INTERSECT",VERTEX,{"disambiguationData":[OD(1.0)],"derivedFrom":[subQ0,sQuery(id+"F0.wireOp",EDGE,"E6.2.0")]}),-1.0]])],"derivedFrom":subQ0})])],"isStart":false});}
            var Q33;
            {var subQ0=sQuery(id+"F0.wireOp",EDGE,"E1");Q33=makeQuery(id+"F1.opExtrude","CAP_EDGE",EDGE,{"disambiguationData":[OSD([subQ0]),TDD([makeQuery(id+"F0.imprint","IMPRINT",EDGE,{"disambiguationData":[TD([[makeQuery(id+"F0.imprint","INTERSECT",VERTEX,{"disambiguationData":[OD(1.0)],"derivedFrom":[subQ0,sQuery(id+"F0.wireOp",EDGE,"E5")]}),-1.0]])],"derivedFrom":subQ0})])],"isStart":false});}
            var Q34;
            {var subQ0=sQuery(id+"F0.wireOp",EDGE,"E5");Q34=makeQuery(id+"F1.opExtrude","CAP_EDGE",EDGE,{"disambiguationData":[OSD([subQ0]),TDD([makeQuery(id+"F0.imprint","IMPRINT",EDGE,{"disambiguationData":[TD([[makeQuery(id+"F0.imprint","INTERSECT",VERTEX,{"disambiguationData":[OD(1.0)],"derivedFrom":[sQuery(id+"F0.wireOp",EDGE,"E1"),subQ0]}),1.0]])],"derivedFrom":subQ0})])],"isStart":false});}
            var Q35;
            {var subQ0=sQuery(id+"F0.wireOp",EDGE,"E1");Q35=makeQuery(id+"F1.opExtrude","CAP_EDGE",EDGE,{"disambiguationData":[OSD([subQ0]),TDD([makeQuery(id+"F0.imprint","IMPRINT",EDGE,{"disambiguationData":[TD([[makeQuery(id+"F0.imprint","INTERSECT",VERTEX,{"disambiguationData":[OD(1.0)],"derivedFrom":[subQ0,sQuery(id+"F0.wireOp",EDGE,"E5")]}),-1.0]])],"derivedFrom":subQ0})])],"isStart":true});}
            var Q36;
            {var subQ0=sQuery(id+"F0.wireOp",EDGE,"E5");Q36=makeQuery(id+"F1.opExtrude","CAP_EDGE",EDGE,{"disambiguationData":[OSD([subQ0]),TDD([makeQuery(id+"F0.imprint","IMPRINT",EDGE,{"disambiguationData":[TD([[makeQuery(id+"F0.imprint","INTERSECT",VERTEX,{"disambiguationData":[OD(1.0)],"derivedFrom":[sQuery(id+"F0.wireOp",EDGE,"E1"),subQ0]}),1.0]])],"derivedFrom":subQ0})])],"isStart":true});}
            fillet(context, id + "F3", {"entities" : qUnion([Q0, Q1, Q2, Q3, Q4, Q5, Q6, Q7, Q8, Q9, Q10, Q11, Q12, Q13, Q14, Q15, Q16, Q17, Q18, Q19, Q20, Q21, Q22, Q23, Q24, Q25, Q26, Q27, Q28, Q29, Q30, Q31, Q32, Q33, Q34, Q35, Q36]), "radius" : 1 * mm, "tangentPropagation" : true, "allowEdgeOverflow" : false});
        }
    });
